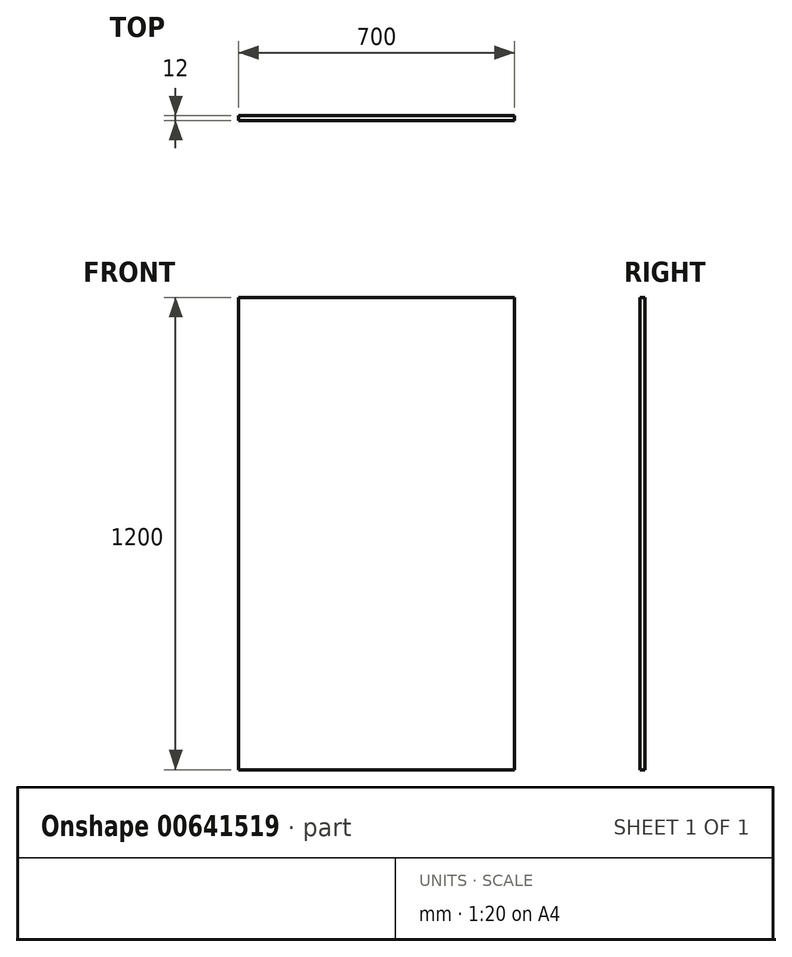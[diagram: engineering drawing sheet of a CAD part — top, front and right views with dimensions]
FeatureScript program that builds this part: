
annotation { "Feature Type Name" : "Feature", "Feature Type Description" : "" }
export const myFeature = defineFeature(function(context is Context, id is Id, definition is map)
    precondition{}
    {
        {
            var Q0;
            Q0=qCreatedBy(makeId("Top.planeOp"),FACE);
            var sketch = newSketch(context, id + "F0", { "sketchPlane" : qUnion([Q0])});
            skLineSegment(sketch, "E0.bottom", {"start": v(0, 0) * mm, "end": v(700, 0) * mm});
            skLineSegment(sketch, "E0.top", {"start": v(0, 12) * mm, "end": v(700, 12) * mm});
            skLineSegment(sketch, "E0.left", {"start": v(0, 0) * mm, "end": v(0, 12) * mm});
            skLineSegment(sketch, "E0.right", {"start": v(700, 0) * mm, "end": v(700, 12) * mm});
            skSolve(sketch);
        }
        {
            var Q0;
            Q0=makeQuery(id+"F0.imprint","IMPRINT",FACE,{"disambiguationData":[TD([[makeQuery(id+"F0.imprint","IMPRINT",EDGE,{"derivedFrom":sQuery(id+"F0.wireOp",EDGE,"E0.bottom")}),1.0]])]});
            extrude(context, id + "F1", {"entities" : qUnion([Q0]), "depth" : 1200 * mm, "offsetDistance" : 25 * mm});
        }
    });
